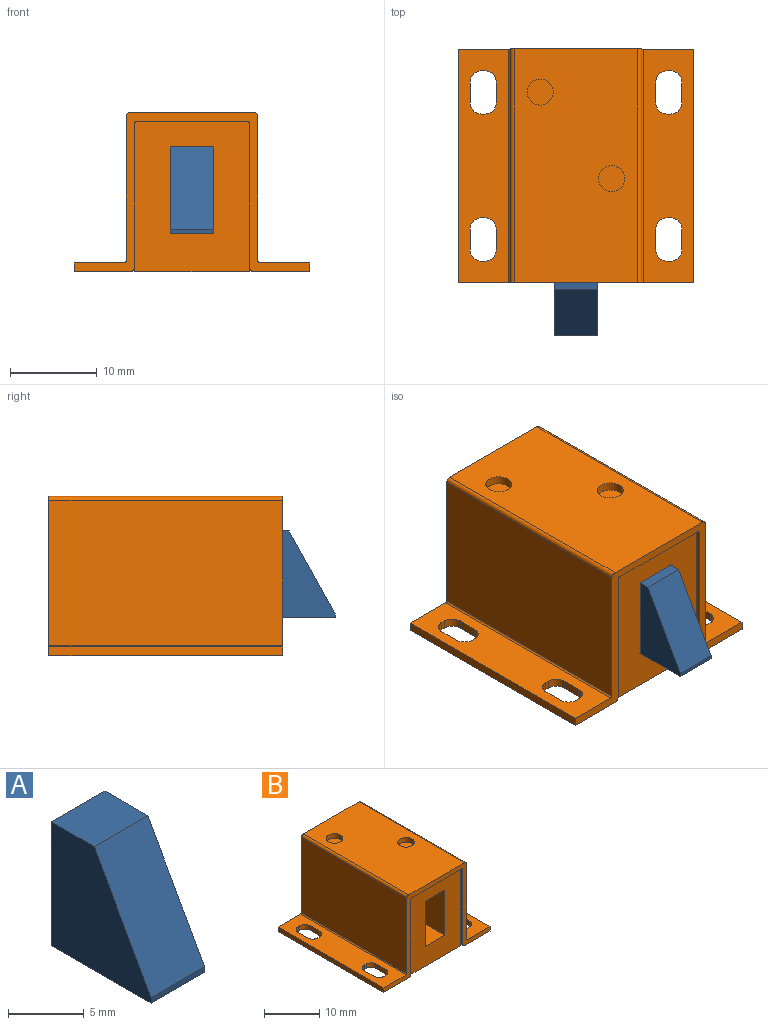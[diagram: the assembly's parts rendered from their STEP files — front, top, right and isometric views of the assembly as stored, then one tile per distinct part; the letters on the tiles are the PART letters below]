
ASSEMBLY  parts=2 mates=1
PART A: 7 faces, bbox 5x9.3x10 mm
  f0: plane 9.3x5mm, normal (0,0,-1), area 46.5mm2, adj f1,f3,f4,f6
  f1: plane 10x9.3mm, normal (1,0,0), area 67.7mm2, adj f0,f2,f4,f5,f6
  f2: plane 5x4mm, normal (0,0,1), area 20mm2, adj f1,f3,f4,f5
  f3: plane 10x9.3mm, normal (-1,0,0), area 67.7mm2, adj f0,f2,f4,f5,f6
  f4: plane 10x5mm, normal (0,1,0), area 50mm2, adj f0,f1,f2,f3
  f5: plane 9.56x5.3mm, normal (0,-0.87,0.48), area 54.7mm2, adj f1,f2,f3,f6
  f6: plane 5x0.44mm, normal (0,-1,0), area 2.2mm2, adj f0,f1,f3,f5
PART B: 73 faces, bbox 27.3x27x18.4 mm
  f0: plane 17.4x13.25mm, normal (0,-1,0), area 180.5mm2, adj f1,f2,f3,f4,f25,f64,f65,f66
  f1: plane 12.65x0.5mm, normal (0,0,-1), area 6.3mm2, adj f0,f4,f25,f27
  f2: plane 16.6x0.5mm, normal (-1,0,0), area 8.3mm2, adj f0,f4,f11,f27
  f3: plane 16.6x0.5mm, normal (1,0,0), area 8.3mm2, adj f0,f23,f25,f27
  f4: cylinder r=0.3mm len=0.5mm, axis (0,-1,0), area 0.2mm2, adj f0,f1,f2,f27
  f5: cylinder r=0.3mm len=0.5mm, axis (0,-1,0), area 0.2mm2, adj f8,f24,f26,f67
  f6: plane 27x6.5mm, normal (0,0,-1), area 148.4mm2, adj f11,f12,f26,f27,f28,f29,f30,f31
  f7: plane 27x5.8mm, normal (0,0,1), area 129.5mm2, adj f12,f13,f26,f27,f28,f29,f30,f31
  f8: plane 12.65x0.5mm, normal (0,0,-1), area 6.3mm2, adj f5,f9,f26,f67
  f9: cylinder r=0.3mm len=0.5mm, axis (0,-1,0), area 0.2mm2, adj f8,f10,f26,f67
  f10: plane 16.6x0.5mm, normal (-1,0,0), area 8.3mm2, adj f9,f11,f26,f67
  f11: cylinder r=0.5mm len=27mm, axis (0,-1,0), area 21.2mm2, adj f2,f6,f10,f26,f27,f64
  f12: plane 27x1mm, normal (1,0,0), area 27mm2, adj f6,f7,f26,f27
  f13: cylinder r=0.2mm len=27mm, axis (0,-1,0), area 8.5mm2, adj f7,f14,f26,f27
  f14: plane 27x16.7mm, normal (1,0,0), area 450.9mm2, adj f13,f15,f26,f27
  f15: cylinder r=0.5mm len=27mm, axis (0,-1,0), area 21.2mm2, adj f14,f16,f26,f27
  f16: plane 27x14.25mm, normal (0,0,1), area 370.6mm2, adj f15,f17,f26,f27,f60,f61
  f17: cylinder r=0.5mm len=27mm, axis (0,-1,0), area 21.2mm2, adj f16,f18,f26,f27
  f18: plane 27x16.7mm, normal (-1,0,0), area 450.9mm2, adj f17,f19,f26,f27
  f19: cylinder r=0.2mm len=27mm, axis (0,-1,0), area 8.5mm2, adj f18,f20,f26,f27
  f20: plane 27x5.8mm, normal (0,0,1), area 129.5mm2, adj f19,f21,f26,f27,f44,f45,f46,f47
  f21: plane 27x1mm, normal (-1,0,0), area 27mm2, adj f20,f22,f26,f27
  f22: plane 27x6.5mm, normal (0,0,-1), area 148.4mm2, adj f21,f23,f26,f27,f44,f45,f46,f47
  f23: cylinder r=0.5mm len=27mm, axis (0,-1,0), area 21.2mm2, adj f3,f22,f24,f26,f27,f65
  f24: plane 16.6x0.5mm, normal (1,0,0), area 8.3mm2, adj f5,f23,f26,f67
  f25: cylinder r=0.3mm len=0.5mm, axis (0,-1,0), area 0.2mm2, adj f0,f1,f3,f27
  f26: plane 27.25x18.4mm, normal (0,1,0), area 61.9mm2, adj f5,f6,f7,f8,f9,f10,f11,f12
  f27: plane 27.25x18.4mm, normal (0,-1,0), area 61.9mm2, adj f1,f2,f3,f4,f6,f7,f11,f12
  f28: cylinder r=1.3mm len=1.3mm, axis (0,0,1), area 2mm2, adj f6,f7,f29,f35
  f29: plane 2.4x1mm, normal (-1,0,0), area 2.4mm2, adj f6,f7,f28,f30
  f30: cylinder r=1.3mm len=1.3mm, axis (0,0,1), area 2mm2, adj f6,f7,f29,f31
  f31: plane 1x0.4mm, normal (0,-1,0), area 0.4mm2, adj f6,f7,f30,f32
  f32: cylinder r=1.3mm len=1.3mm, axis (0,0,1), area 2mm2, adj f6,f7,f31,f33
  f33: plane 2.4x1mm, normal (1,0,0), area 2.4mm2, adj f6,f7,f32,f34
  f34: cylinder r=1.3mm len=1.3mm, axis (0,0,1), area 2mm2, adj f6,f7,f33,f35
  f35: plane 1x0.4mm, normal (0,1,0), area 0.4mm2, adj f6,f7,f28,f34
  f36: plane 1x0.4mm, normal (0,1,0), area 0.4mm2, adj f6,f7,f37,f43
  f37: cylinder r=1.3mm len=1.3mm, axis (0,0,1), area 2mm2, adj f6,f7,f36,f38
  f38: plane 2.4x1mm, normal (-1,0,0), area 2.4mm2, adj f6,f7,f37,f39
  f39: cylinder r=1.3mm len=1.3mm, axis (0,0,1), area 2mm2, adj f6,f7,f38,f40
  f40: plane 1x0.4mm, normal (0,-1,0), area 0.4mm2, adj f6,f7,f39,f41
  f41: cylinder r=1.3mm len=1.3mm, axis (0,0,1), area 2mm2, adj f6,f7,f40,f42
  f42: plane 2.4x1mm, normal (1,0,0), area 2.4mm2, adj f6,f7,f41,f43
  f43: cylinder r=1.3mm len=1.3mm, axis (0,0,1), area 2mm2, adj f6,f7,f36,f42
  f44: cylinder r=1.3mm len=1.3mm, axis (0,0,1), area 2mm2, adj f20,f22,f45,f51
  f45: plane 1x0.4mm, normal (0,1,0), area 0.4mm2, adj f20,f22,f44,f46
  f46: cylinder r=1.3mm len=1.3mm, axis (0,0,1), area 2mm2, adj f20,f22,f45,f47
  f47: plane 2.4x1mm, normal (-1,0,0), area 2.4mm2, adj f20,f22,f46,f48
  f48: cylinder r=1.3mm len=1.3mm, axis (0,0,1), area 2mm2, adj f20,f22,f47,f49
  f49: plane 1x0.4mm, normal (0,-1,0), area 0.4mm2, adj f20,f22,f48,f50
  f50: cylinder r=1.3mm len=1.3mm, axis (0,0,1), area 2mm2, adj f20,f22,f49,f51
  f51: plane 2.4x1mm, normal (1,0,0), area 2.4mm2, adj f20,f22,f44,f50
  f52: plane 1x0.4mm, normal (0,1,0), area 0.4mm2, adj f20,f22,f53,f59
  f53: cylinder r=1.3mm len=1.3mm, axis (0,0,1), area 2mm2, adj f20,f22,f52,f54
  f54: plane 2.4x1mm, normal (-1,0,0), area 2.4mm2, adj f20,f22,f53,f55
  f55: cylinder r=1.3mm len=1.3mm, axis (0,0,1), area 2mm2, adj f20,f22,f54,f56
  f56: plane 1x0.4mm, normal (0,-1,0), area 0.4mm2, adj f20,f22,f55,f57
  f57: cylinder r=1.3mm len=1.3mm, axis (0,0,1), area 2mm2, adj f20,f22,f56,f58
  f58: plane 2.4x1mm, normal (1,0,0), area 2.4mm2, adj f20,f22,f57,f59
  f59: cylinder r=1.3mm len=1.3mm, axis (0,0,1), area 2mm2, adj f20,f22,f52,f58
  f60: cylinder r=1.5mm len=3mm, axis (0,0,1), area 9.4mm2, adj f16,f63
  f61: cylinder r=1.5mm len=3mm, axis (0,0,1), area 9.4mm2, adj f16,f62
  f62: plane 3x3mm, normal (0,0,1), area 7.1mm2, adj f61
  f63: plane 3x3mm, normal (0,0,1), area 7.1mm2, adj f60
  f64: plane 26x0.5mm, normal (1,0,0), area 13mm2, adj f0,f11,f66,f67
  f65: plane 26x0.5mm, normal (-1,0,0), area 13mm2, adj f0,f23,f66,f67
  f66: plane 26x13.25mm, normal (0,0,-1), area 344.5mm2, adj f0,f64,f65,f67
  f67: plane 17.4x13.25mm, normal (0,1,0), area 230.5mm2, adj f5,f8,f9,f10,f24,f64,f65,f66
  f68: plane 9.3x5mm, normal (0,0,1), area 46.5mm2, adj f0,f69,f71,f72
  f69: plane 10x9.3mm, normal (-1,0,0), area 93mm2, adj f0,f68,f70,f72
  f70: plane 9.3x5mm, normal (0,0,-1), area 46.5mm2, adj f0,f69,f71,f72
  f71: plane 10x9.3mm, normal (1,0,0), area 93mm2, adj f0,f68,f70,f72
  f72: plane 10x5mm, normal (0,-1,0), area 50mm2, adj f68,f69,f70,f71
PLACE A t=(0,-6.56,0)mm
PLACE B at identity fixed
MATE slider A.f6 <-> B.f0  axis (0,1,0) through (2.5,-19.56,4.4)mm
